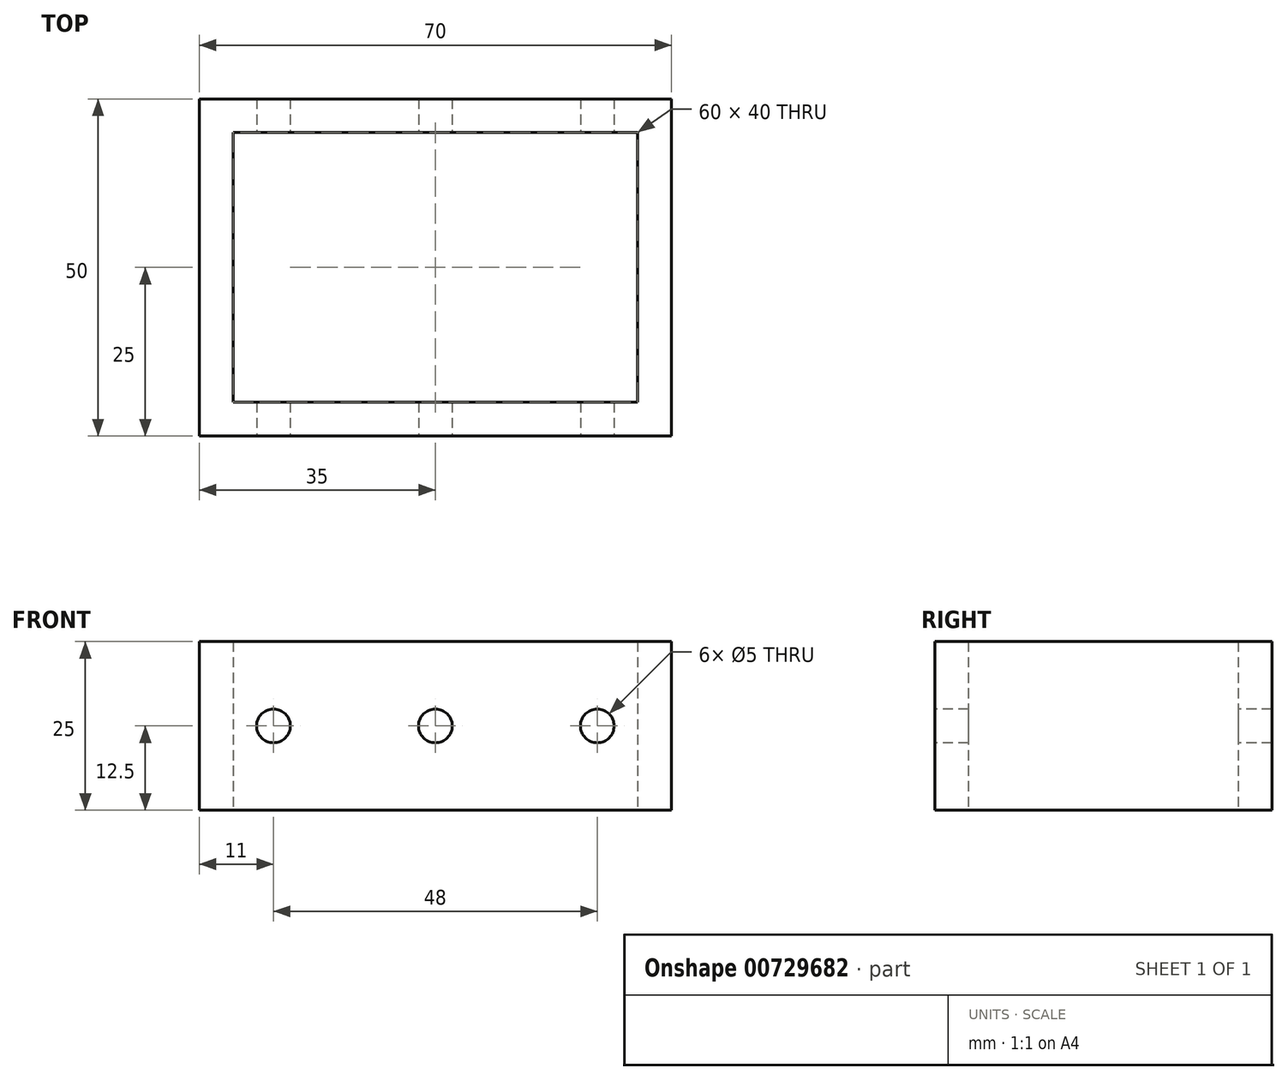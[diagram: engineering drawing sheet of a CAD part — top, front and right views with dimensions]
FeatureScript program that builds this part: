
annotation { "Feature Type Name" : "Feature", "Feature Type Description" : "" }
export const myFeature = defineFeature(function(context is Context, id is Id, definition is map)
    precondition{}
    {
        {
            var Q0;
            Q0=qCreatedBy(makeId("Top.planeOp"),FACE);
            var sketch = newSketch(context, id + "F0", { "sketchPlane" : qUnion([Q0])});
            skLineSegment(sketch, "E0.bottom", {"start": v(-35, 25) * mm, "end": v(35, 25) * mm});
            skLineSegment(sketch, "E0.top", {"start": v(-35, -25) * mm, "end": v(35, -25) * mm});
            skLineSegment(sketch, "E0.left", {"start": v(-35, 25) * mm, "end": v(-35, -25) * mm});
            skLineSegment(sketch, "E0.right", {"start": v(35, 25) * mm, "end": v(35, -25) * mm});
            skPoint(sketch, "E0.middle", {"position": v(0, 0) * mm});
            skLineSegment(sketch, "E1.bottom", {"start": v(-30, 20) * mm, "end": v(30, 20) * mm});
            skLineSegment(sketch, "E1.top", {"start": v(-30, -20) * mm, "end": v(30, -20) * mm});
            skLineSegment(sketch, "E1.left", {"start": v(-30, 20) * mm, "end": v(-30, -20) * mm});
            skLineSegment(sketch, "E1.right", {"start": v(30, 20) * mm, "end": v(30, -20) * mm});
            skSolve(sketch);
        }
        {
            var Q0;
            Q0=makeQuery(id+"F0.imprint","IMPRINT",FACE,{"disambiguationData":[TD([[makeQuery(id+"F0.imprint","IMPRINT",EDGE,{"derivedFrom":sQuery(id+"F0.wireOp",EDGE,"E0.bottom")}),-1.0]])]});
            extrude(context, id + "F1", {"entities" : qUnion([Q0]), "endBound" : BoundingType.SYMMETRIC, "depth" : 25 * mm, "offsetDistance" : 25 * mm});
        }
        {
            var Q0;
            Q0=makeQuery(id+"F1.opExtrude","SWEPT_FACE",FACE,{"disambiguationData":[OSD([sQuery(id+"F0.wireOp",EDGE,"E0.top")])]});
            var sketch = newSketch(context, id + "F2", { "sketchPlane" : qUnion([Q0])});
            skCircle(sketch, "E2", {"center": v(-24, 0) * mm, "radius": 2.5 * mm});
            skCircle(sketch, "E3", {"center": v(0, 0) * mm, "radius": 2.5 * mm});
            skCircle(sketch, "E4", {"center": v(24, 0) * mm, "radius": 2.5 * mm});
            skSolve(sketch);
        }
        {
            var Q0;
            Q0=makeQuery(id+"F2.imprint","IMPRINT",FACE,{"disambiguationData":[TD([[makeQuery(id+"F2.imprint","IMPRINT",EDGE,{"derivedFrom":sQuery(id+"F2.wireOp",EDGE,"E2")}),1.0]])]});
            var Q1;
            Q1=makeQuery(id+"F2.imprint","IMPRINT",FACE,{"disambiguationData":[TD([[makeQuery(id+"F2.imprint","IMPRINT",EDGE,{"derivedFrom":sQuery(id+"F2.wireOp",EDGE,"E3")}),1.0]])]});
            var Q2;
            Q2=makeQuery(id+"F2.imprint","IMPRINT",FACE,{"disambiguationData":[TD([[makeQuery(id+"F2.imprint","IMPRINT",EDGE,{"derivedFrom":sQuery(id+"F2.wireOp",EDGE,"E4")}),1.0]])]});
            extrude(context, id + "F3", {"entities" : qUnion([Q0, Q1, Q2]), "operationType" : NewBodyOperationType.REMOVE, "endBound" : BoundingType.THROUGH_ALL, "oppositeDirection" : true, "depth" : 25 * mm, "offsetDistance" : 25 * mm});
        }
    });
